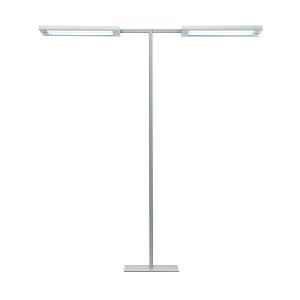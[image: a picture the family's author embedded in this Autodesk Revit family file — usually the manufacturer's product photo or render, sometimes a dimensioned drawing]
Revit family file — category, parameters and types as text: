
# Revit family: lavigo_-_dps_30000_840_r_g2a_-_twin-t_00808553_5835
name_source: partatom
category: Lighting Fixtures
units: mm (PartAtom-declared; Revit-internal decimal feet)

## family parameters
Cut with Voids When Loaded = No
Host = Face
Light Source = No
Part Type = Normal
Room Calculation Point = No
Round Connector Dimension = Use Diameter
Shared = No

## types (1)
- LAVIGO - DPS 30000/840/R/G2A - TWIN-T (1 x LED, 15250 lm, 4000K)
    Apparent Load = 210 VA
    Approval mark = CE
    CIE Flux Codes = 60 87 97 11 100
    Color Rendering = 80-89
    Color Temperature = 4000K
    Default Elevation = 1800 mm
    Description = DPS 30000/840/R/G2A|Free-standing luminaire|light source: LED|work equipment: Electronic ballast|connected load: 220-240 V, 50/60 Hz|Power consumption: approx. 210 W|standby: approx. 0,50|power factor: approx. 0,966|luminous flux: 30500 lm|luminous efficacy: 145 lm/W|light distribution: Direct/indirect|direct ratio: approx. 12 %|colour temperature: Cold white, ca. 4000 K|color rendering index (CRI): >= 80|chromaticity tolerance:  3 SDCM|technology: Presence and daylight sensor control (PIR)|operation: Multi-function switch, Touch-LED|luminaire body|material: Steel/plastic|surface: Painted|colour: Silver metallic|lamp cover: Acrylic (PMMA), Satine|tubular section|material: Steel tube|surface: Painted|Form: Tubular section upright|colour of tubular section: Silver metallic|luminaire base|Form: Rectangular flat|weight (net): approx. 28.4 kg|mains lead: 3.00 m Mains plug CEE 7/VII|Fastening: Floor standing base|decorative contrast side parts: Flint grey|glare control: Prism aperture|luminance(L65): <= 3000 cd/m|unified glare rating(4H 8H): <=  16|special features: Luminaire head detachable, Asymmetric radiation, Direct light component with edge light and light-guide technology for homogenous light exit, Flicker-free, Integrated light and presence sensor PIR, Retrofittable with TALK module, Separated, direct and indirect light individually adjustable|
    Height = 36 mm
    Lamp = 1 x LED
    Lamp Light Flux = 15250 lm
    Lamp count = 1
    Length = 675 mm
    Luminous efficacy = 145 lm/W
    Manufacturer = Waldmann
    ModVariant = No
    Model = 00808553
    Mounting Place = Floor
    Mounting Type = Freestanding
    Number of Poles = 1
    OnlyDefault = Yes
    Power Factor = 1
    Product Name = LAVIGO - DPS 30000/840/R/G2A - TWIN-T
    Product group = Free standing luminaire
    ProductGroupID = 13
    Protection Class = Protection class I
    Protection Degree = IP 20
    RLX_Detail_Level = 1
    RLX_Emergency_Light_Flux = 0 lm
    RLX_Emergency_Type = 0
    RLX_Emergency_Type_DB = No
    RlxData = <blob elided: 38697 chars, md5=4b5c66fb>
    Socket = socket
    Standby Power = 0 W
    System Light Flux = 30500 lm
    System Power = 210 W
    Type Comments = Product without accessories
    Type Image = 121712000-00642698.jpg
    URL = http://relux.com
    VarID = ---
    Voltage = 0 V
    Weight = 0.00 kg
    Width = 350 mm

## geometry (parser evidence)
native form markers: Blend x4, Sweep x18
no freeform markers — native parametric forms only
